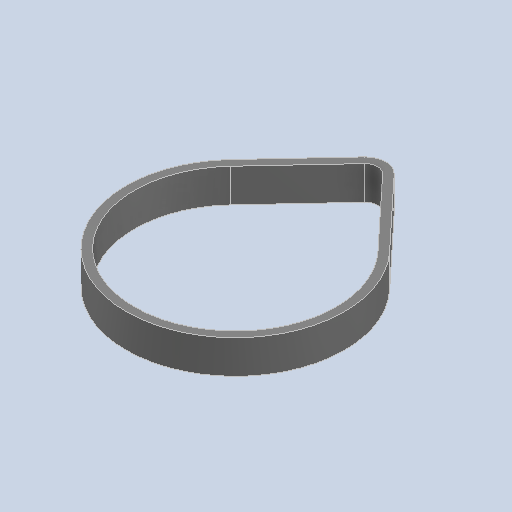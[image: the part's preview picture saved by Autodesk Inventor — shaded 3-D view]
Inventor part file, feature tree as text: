
AUTODESK INVENTOR PART (.ipt)
format: ipt  version: 2023.2 (Build 272271000, 271)  size: 97,792 bytes
history: native  units: in
note: dims shown in document units (in); Inventor stores cm internally (conversion verified against a paired STEP export)
features: extrude x1
ambient origin geometry x8: Origin, YZ Plane, XZ Plane, XY Plane, X Axis, Y Axis, Z Axis, Center Point
bodies: Solid1 (feature_tree)
feature tree (1):
  extrude  "Extrude-Thin1"  [1 undecoded]
note: 1 required parameter value undecoded (feature->parameter linkage not recoverable at this tier; creation-order binding heuristic only, values carry confidence <= 0.55)
